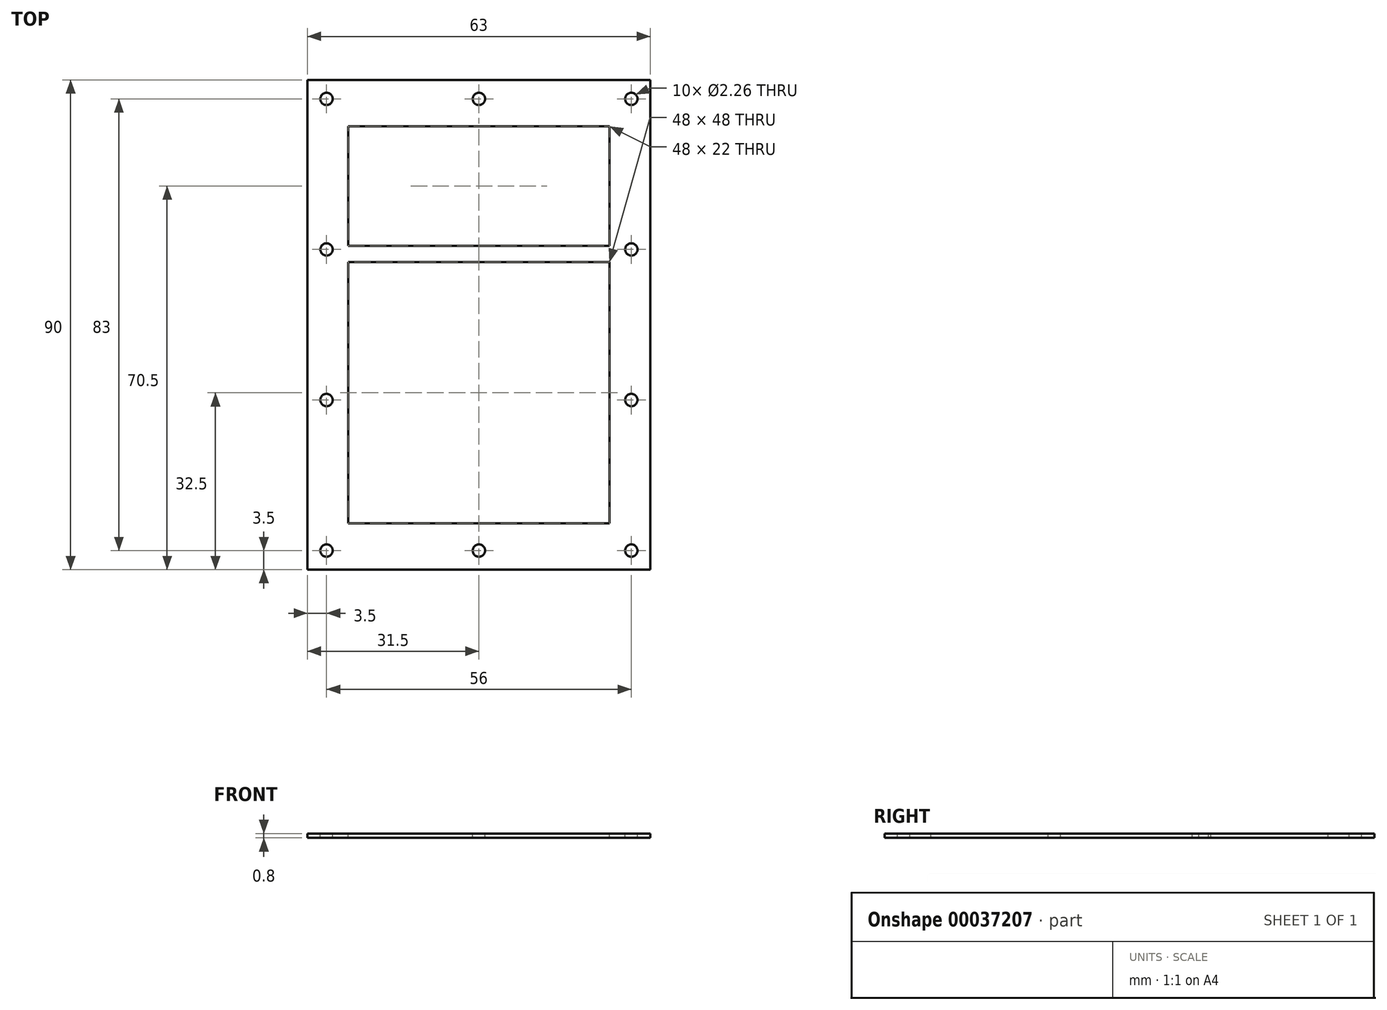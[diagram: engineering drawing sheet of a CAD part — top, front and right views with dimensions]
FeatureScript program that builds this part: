
annotation { "Feature Type Name" : "Feature", "Feature Type Description" : "" }
export const myFeature = defineFeature(function(context is Context, id is Id, definition is map)
    precondition{}
    {
        {
            var Q0;
            Q0=qCreatedBy(makeId("Top.planeOp"),FACE);
            var sketch = newSketch(context, id + "F0", { "sketchPlane" : qUnion([Q0])});
            skLineSegment(sketch, "E0.rect.bottom", {"start": v(31.5, 45) * mm, "end": v(-31.5, 45) * mm});
            skLineSegment(sketch, "E0.rect.top", {"start": v(31.5, -45) * mm, "end": v(-31.5, -45) * mm});
            skLineSegment(sketch, "E0.rect.left", {"start": v(31.5, 45) * mm, "end": v(31.5, -45) * mm});
            skLineSegment(sketch, "E0.rect.right", {"start": v(-31.5, 45) * mm, "end": v(-31.5, -45) * mm});
            skPoint(sketch, "E0.rect.middle", {"position": v(0, 0) * mm});
            skSolve(sketch);
        }
        {
            var Q0;
            Q0=makeQuery(id+"F0.imprint","IMPRINT",FACE,{"disambiguationData":[TD([[makeQuery(id+"F0.imprint","IMPRINT",EDGE,{"derivedFrom":sQuery(id+"F0.wireOp",EDGE,"E0.rect.bottom")}),1.0]])]});
            extrude(context, id + "F1", {"entities" : qUnion([Q0]), "depth" : .8 * mm});
        }
        {
            var Q0;
            Q0=makeQuery(id+"F1.opExtrude","CAP_FACE",FACE,{"disambiguationData":[OSD([sQuery(id+"F0.wireOp",EDGE,"E0.rect.bottom"),sQuery(id+"F0.wireOp",EDGE,"E0.rect.top"),sQuery(id+"F0.wireOp",EDGE,"E0.rect.left"),sQuery(id+"F0.wireOp",EDGE,"E0.rect.right")])],"isStart":false});
            var sketch = newSketch(context, id + "F2", { "sketchPlane" : qUnion([Q0])});
            skLineSegment(sketch, "E1.rect.bottom", {"start": v(25, 37.5) * mm, "end": v(-25, 37.5) * mm});
            skLineSegment(sketch, "E1.rect.top", {"start": v(25, -37.5) * mm, "end": v(-25, -37.5) * mm});
            skLineSegment(sketch, "E1.rect.left", {"start": v(25, 37.5) * mm, "end": v(25, -37.5) * mm});
            skLineSegment(sketch, "E1.rect.right", {"start": v(-25, 37.5) * mm, "end": v(-25, -37.5) * mm});
            skPoint(sketch, "E1.rect.middle", {"position": v(0, 0) * mm});
            skLineSegment(sketch, "E2", {"start": v(-25, 12.5) * mm, "end": v(25, 12.5) * mm});
            skSolve(sketch);
        }
        {
            var Q0;
            {var subQ4=sQuery(id+"F2.wireOp",EDGE,"E1.rect.bottom");Q0=makeQuery(id+"F2.imprint","IMPRINT",FACE,{"disambiguationData":[TD([[makeQuery(id+"F2.imprint","IMPRINT",EDGE,{"derivedFrom":subQ4}),-1.0]])]});}
            var sketch = newSketch(context, id + "F3", { "sketchPlane" : qUnion([Q0])});
            skLineSegment(sketch, "E3.rect.bottom", {"start": v(28, 41.5) * mm, "end": v(-28, 41.5) * mm, "construction": true});
            skLineSegment(sketch, "E3.rect.top", {"start": v(28, -41.5) * mm, "end": v(-28, -41.5) * mm, "construction": true});
            skLineSegment(sketch, "E3.rect.left", {"start": v(28, 41.5) * mm, "end": v(28, -41.5) * mm, "construction": true});
            skLineSegment(sketch, "E3.rect.right", {"start": v(-28, 41.5) * mm, "end": v(-28, -41.5) * mm, "construction": true});
            skPoint(sketch, "E3.rect.middle", {"position": v(0, 0) * mm});
            skCircle(sketch, "E4", {"center": v(-28, 41.5) * mm, "radius": 1.13 * mm});
            skCircle(sketch, "E5", {"center": v(-28, -41.5) * mm, "radius": 1.13 * mm});
            skCircle(sketch, "E6", {"center": v(28, -41.5) * mm, "radius": 1.13 * mm});
            skCircle(sketch, "E7", {"center": v(28, 41.5) * mm, "radius": 1.13 * mm});
            skPoint(sketch, "E8", {"position": v(0, 41.5) * mm});
            skCircle(sketch, "E9", {"center": v(0, 41.5) * mm, "radius": 1.13 * mm});
            skPoint(sketch, "E10", {"position": v(0, -41.5) * mm});
            skCircle(sketch, "E11", {"center": v(0, -41.5) * mm, "radius": 1.13 * mm});
            skPoint(sketch, "E12", {"position": v(-28, 13.83) * mm});
            skPoint(sketch, "E13", {"position": v(-28, -13.83) * mm});
            skPoint(sketch, "E14", {"position": v(28, 13.83) * mm});
            skPoint(sketch, "E15", {"position": v(28, -13.83) * mm});
            skCircle(sketch, "E16", {"center": v(-28, 13.83) * mm, "radius": 1.13 * mm});
            skCircle(sketch, "E17", {"center": v(-28, -13.83) * mm, "radius": 1.13 * mm});
            skCircle(sketch, "E18", {"center": v(28, 13.83) * mm, "radius": 1.13 * mm});
            skCircle(sketch, "E19", {"center": v(28, -13.83) * mm, "radius": 1.13 * mm});
            skSolve(sketch);
        }
        {
            var Q0;
            Q0 = qSketchRegion(id + "F3", true);
            extrude(context, id + "F4", {"entities" : qUnion([Q0]), "operationType" : NewBodyOperationType.REMOVE, "oppositeDirection" : true, "depth" : 25 * mm});
        }
        {
            var Q0;
            {var subQ4=sQuery(id+"F2.wireOp",EDGE,"E1.rect.bottom");Q0=makeQuery(id+"F2.imprint","IMPRINT",FACE,{"disambiguationData":[TD([[makeQuery(id+"F2.imprint","IMPRINT",EDGE,{"derivedFrom":subQ4}),-1.0]])]});}
            var sketch = newSketch(context, id + "F5", { "sketchPlane" : qUnion([Q0])});
            skLineSegment(sketch, "E20.rect.bottom", {"start": v(24, 36.5) * mm, "end": v(-24, 36.5) * mm});
            skLineSegment(sketch, "E20.rect.top", {"start": v(24, 14.5) * mm, "end": v(-24, 14.5) * mm});
            skLineSegment(sketch, "E20.rect.left", {"start": v(24, 36.5) * mm, "end": v(24, 14.5) * mm});
            skLineSegment(sketch, "E20.rect.right", {"start": v(-24, 36.5) * mm, "end": v(-24, 14.5) * mm});
            skLineSegment(sketch, "E21.bottom", {"start": v(-24, 11.5) * mm, "end": v(24, 11.5) * mm});
            skLineSegment(sketch, "E21.top", {"start": v(-24, -36.5) * mm, "end": v(24, -36.5) * mm});
            skLineSegment(sketch, "E21.left", {"start": v(-24, 11.5) * mm, "end": v(-24, -36.5) * mm});
            skLineSegment(sketch, "E21.right", {"start": v(24, 11.5) * mm, "end": v(24, -36.5) * mm});
            skSolve(sketch);
        }
        {
            var Q0;
            Q0 = qSketchRegion(id + "F5", true);
            extrude(context, id + "F6", {"entities" : qUnion([Q0]), "operationType" : NewBodyOperationType.REMOVE, "oppositeDirection" : true, "depth" : 25 * mm});
        }
    });
